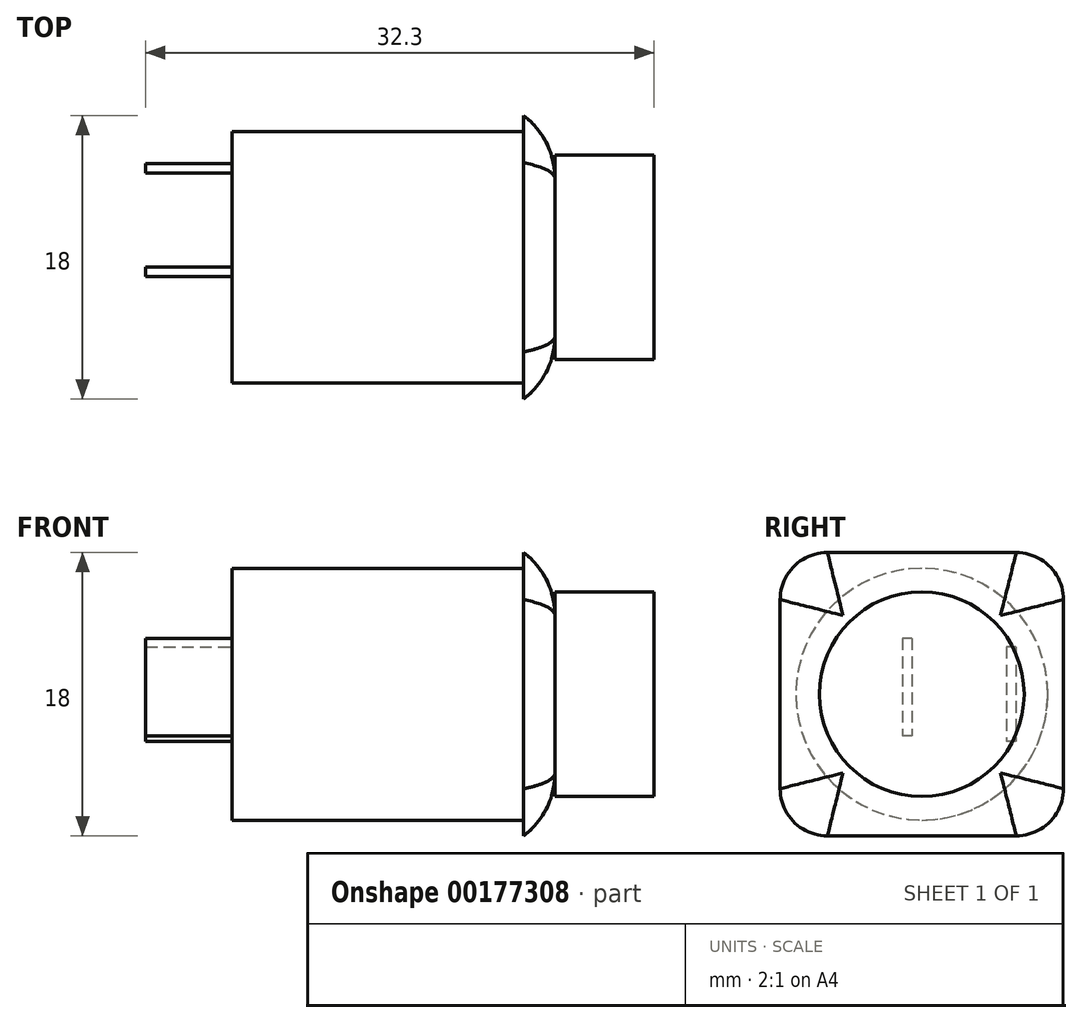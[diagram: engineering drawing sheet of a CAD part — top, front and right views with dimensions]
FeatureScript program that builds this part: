
annotation { "Feature Type Name" : "Feature", "Feature Type Description" : "" }
export const myFeature = defineFeature(function(context is Context, id is Id, definition is map)
    precondition{}
    {
        {
            var Q0;
            Q0=qCreatedBy(makeId("Right.planeOp"),FACE);
            var sketch = newSketch(context, id + "F0", { "sketchPlane" : qUnion([Q0])});
            skLineSegment(sketch, "E0.bottom", {"start": v(-9, 9) * mm, "end": v(9, 9) * mm});
            skLineSegment(sketch, "E0.top", {"start": v(-9, -9) * mm, "end": v(9, -9) * mm});
            skLineSegment(sketch, "E0.left", {"start": v(-9, 9) * mm, "end": v(-9, -9) * mm});
            skLineSegment(sketch, "E0.right", {"start": v(9, 9) * mm, "end": v(9, -9) * mm});
            skPoint(sketch, "E0.middle", {"position": v(0, 0) * mm});
            skSolve(sketch);
        }
        {
            var Q0;
            Q0 = qSketchRegion(id + "F0", true);
            extrude(context, id + "F1", {"entities" : qUnion([Q0]), "depth" : 2 * mm});
        }
        {
            var Q0;
            Q0=makeQuery(id+"F1.opExtrude","SWEPT_EDGE",EDGE,{"disambiguationData":[OSD([sQuery(id+"F0.wireOp",EDGE,"E0.bottom"),sQuery(id+"F0.wireOp",EDGE,"E0.left")])]});
            var Q1;
            Q1=makeQuery(id+"F1.opExtrude","SWEPT_EDGE",EDGE,{"disambiguationData":[OSD([sQuery(id+"F0.wireOp",EDGE,"E0.bottom"),sQuery(id+"F0.wireOp",EDGE,"E0.right")])]});
            var Q2;
            Q2=makeQuery(id+"F1.opExtrude","SWEPT_EDGE",EDGE,{"disambiguationData":[OSD([sQuery(id+"F0.wireOp",EDGE,"E0.top"),sQuery(id+"F0.wireOp",EDGE,"E0.left")])]});
            var Q3;
            Q3=makeQuery(id+"F1.opExtrude","SWEPT_EDGE",EDGE,{"disambiguationData":[OSD([sQuery(id+"F0.wireOp",EDGE,"E0.top"),sQuery(id+"F0.wireOp",EDGE,"E0.right")])]});
            fillet(context, id + "F2", {"entities" : qUnion([Q0, Q1, Q2, Q3]), "radius" : 3 * mm, "tangentPropagation" : true, "allowEdgeOverflow" : false});
        }
        {
            var Q0;
            Q0=makeQuery(id+"F1.opExtrude","CAP_FACE",FACE,{"disambiguationData":[OSD([sQuery(id+"F0.wireOp",EDGE,"E0.bottom"),sQuery(id+"F0.wireOp",EDGE,"E0.top"),sQuery(id+"F0.wireOp",EDGE,"E0.left"),sQuery(id+"F0.wireOp",EDGE,"E0.right")])],"isStart":false});
            var sketch = newSketch(context, id + "F3", { "sketchPlane" : qUnion([Q0])});
            skCircle(sketch, "E1", {"center": v(0, 0) * mm, "radius": 6.5 * mm});
            skSolve(sketch);
        }
        {
            var Q0;
            Q0=makeQuery(id+"F3.imprint","IMPRINT",FACE,{"disambiguationData":[TD([[makeQuery(id+"F3.imprint","IMPRINT",EDGE,{"derivedFrom":sQuery(id+"F3.wireOp",EDGE,"E1")}),1.0]])]});
            extrude(context, id + "F4", {"entities" : qUnion([Q0]), "depth" : 6.3 * mm});
        }
        {
            var Q0;
            Q0=makeQuery(id+"F1.opExtrude","CAP_FACE",FACE,{"disambiguationData":[OSD([sQuery(id+"F0.wireOp",EDGE,"E0.bottom"),sQuery(id+"F0.wireOp",EDGE,"E0.top"),sQuery(id+"F0.wireOp",EDGE,"E0.left"),sQuery(id+"F0.wireOp",EDGE,"E0.right")])],"isStart":false});
            fillet(context, id + "F5", {"entities" : qUnion([Q0]), "radius" : 5 * mm, "tangentPropagation" : true, "allowEdgeOverflow" : false});
        }
        {
            var Q0;
            Q0=makeQuery(id+"F1.opExtrude","CAP_FACE",FACE,{"disambiguationData":[OSD([sQuery(id+"F0.wireOp",EDGE,"E0.bottom"),sQuery(id+"F0.wireOp",EDGE,"E0.top"),sQuery(id+"F0.wireOp",EDGE,"E0.left"),sQuery(id+"F0.wireOp",EDGE,"E0.right")])],"isStart":true});
            var sketch = newSketch(context, id + "F6", { "sketchPlane" : qUnion([Q0])});
            skCircle(sketch, "E2", {"center": v(0, 0) * mm, "radius": 8 * mm});
            skSolve(sketch);
        }
        {
            var Q0;
            Q0 = qSketchRegion(id + "F6", true);
            extrude(context, id + "F7", {"entities" : qUnion([Q0]), "operationType" : NewBodyOperationType.ADD, "depth" : 18.5 * mm});
        }
        {
            var Q0;
            Q0=makeQuery(id+"F7.opExtrude","CAP_FACE",FACE,{"disambiguationData":[OSD([sQuery(id+"F6.wireOp",EDGE,"E2")])],"isStart":false});
            var sketch = newSketch(context, id + "F8", { "sketchPlane" : qUnion([Q0])});
            skLineSegment(sketch, "E3.bottom", {"start": v(-5.97, 3.01) * mm, "end": v(-5.37, 3.01) * mm});
            skLineSegment(sketch, "E3.top", {"start": v(-5.97, -2.99) * mm, "end": v(-5.37, -2.99) * mm});
            skLineSegment(sketch, "E3.left", {"start": v(-5.97, 3.01) * mm, "end": v(-5.97, -2.99) * mm});
            skLineSegment(sketch, "E3.right", {"start": v(-5.37, 3.01) * mm, "end": v(-5.37, -2.99) * mm});
            skLineSegment(sketch, "E4.bottom", {"start": v(0.63, 3.55) * mm, "end": v(1.23, 3.55) * mm});
            skLineSegment(sketch, "E4.top", {"start": v(0.63, -2.64) * mm, "end": v(1.23, -2.64) * mm});
            skLineSegment(sketch, "E4.left", {"start": v(0.63, 3.55) * mm, "end": v(0.63, -2.64) * mm});
            skLineSegment(sketch, "E4.right", {"start": v(1.23, 3.55) * mm, "end": v(1.23, -2.64) * mm});
            skSolve(sketch);
        }
        {
            var Q0;
            Q0 = qSketchRegion(id + "F8", true);
            extrude(context, id + "F9", {"entities" : qUnion([Q0]), "operationType" : NewBodyOperationType.ADD, "depth" : 5.5 * mm});
        }
    });
